# Revit family: ERA_LF_WR_DPA-301
name_source: partatom
category: Осветительные приборы
units: mm (PartAtom-declared; Revit-internal decimal feet)

## family parameters
Всегда вертикально = Да
Заголовок OmniClass = Lighting
Источник света = Да
На основе рабочей плоскости = Нет
Номер OmniClass = 23.80.70.00
Общий = Нет
При загрузке вырезать с полостями = Нет
Размер круглого соединителя = Использовать диаметр
Тип детали = Нормальный
Точка расчета площади = Да

## types (1)
- DPA-301-0-65, LED, IP20, 355х136х60 мм (ДхШхВ), 5 Вт, 6500 К, 282 лм, класс защиты II, в комплекте (драйвер на конденсаторах)
    ADSK_Единица измерения = шт.
    ADSK_Завод-изготовитель = ЭРА
    ADSK_Классификация нагрузок = Освещение
    ADSK_Количество фаз = 1
    ADSK_Коэффициент мощности = 0.85
    ADSK_Марка = DPA-301-0-65
    ADSK_Масса = 0.284
    ADSK_Наименование = Светильник, LED, прямоугольный, настенный, IP20, 355х136х60 мм (ДхШхВ), 5 Вт, 6500 К, 282 лм, класс защиты II, в комплекте (драйвер на конденсаторах)
    ADSK_Наименование краткое = Светильник
    ADSK_Напряжение = 230 В
    ADSK_Номинальная мощность = 5 Вт
    ADSK_Обозначение = DPA-301-0-65
    ADSK_Полная мощность = 6 В·А
    ADSK_Примечание = Драйвер на конденсаторах, пластик
    ADSK_Размер_Высота = 60 мм
    ADSK_Размер_Диаметр = 0 мм
    ADSK_Размер_Длина = 355 мм
    ADSK_Размер_Ширина = 136 мм
    URL = https://www.eraworld.ru
    _Корпус_Высота = 60 мм
    _Корпус_Диаметр = 1 мм
    _Корпус_Длина = 355 мм
    _Корпус_Ширина = 136 мм
    _УГО_Диаметр = 3.55 мм
    _УГО_Длина = 3.55 мм
    _УГО_Ширина = 1.36 мм
    Видимая форма излучения при визуализации = Нет
    Геометрия изделия = Прямоугольный
    Излучение по длине прямоугольника = 355 мм
    Излучение по ширине прямоугольника = 136 мм
    Источник света = LED
    Класс защиты = II
    Класс пожароопасности = Нет
    Комплект = Драйвер на конденсаторах
    Разработчик модели = https://www.teslabim.ru
    Светофильтр = 16777215
    Смещение цветовой температуры при затухании лампы = <Нет>
    Степень защиты IP = IP20
    Тип установки = Настенный
    УГО_Масштаб = 100
    Угол наклона = 90,00°
    Файл фотометрической сетки = DPA-301-0-65.ies
    Цвет = Белый
